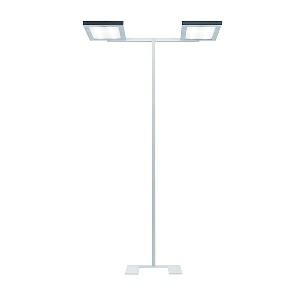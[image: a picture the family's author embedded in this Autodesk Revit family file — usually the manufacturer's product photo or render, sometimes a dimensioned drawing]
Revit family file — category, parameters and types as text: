
# Revit family: lavigo_-_dps_28000_vtl_r_g2_-twin-u_00810632_71ed
name_source: partatom
category: Lighting Fixtures
units: mm (PartAtom-declared; Revit-internal decimal feet)

## family parameters
Cut with Voids When Loaded = No
Host = Face
Light Source = No
Part Type = Normal
Room Calculation Point = No
Round Connector Dimension = Use Diameter
Shared = No

## types (1)
- LAVIGO - DPS 28000/VTL/R/G2 -TWIN-U (1 x LED VTL, 14250 lm, 3000-6500K)
    Apparent Load = 200 VA
    Approval mark = CE
    CIE Flux Codes = 60 87 97 12 100
    Color Rendering = 80-89
    Color Temperature = 3000-6500K
    Default Elevation = 1800 mm
    Description = DPS 28000/VTL/R/G2|Free-standing luminaire|light source: LED  3000-6500 K  Energy efficiency category A/A+/A++|work equipment: Electronic ballast|connected load: 220-240 V, 50/60 Hz|Power consumption: approx. 200 W|standby: approx. 0,50|power factor: approx. 0,966|luminous flux: 28500 lm|luminous efficacy: 142 lm/W|light distribution: Direct/indirect|direct ratio: approx. 12 %|color rendering index (CRI): >= 80|technology: Presence and daylight sensor control (PIR)|operation: Multi-function switch, Touch-LED|luminaire body|material: Steel/plastic|surface: Painted|colour: White|lamp cover: Acrylic (PMMA), Satine|tubular section|material: Steel tube|surface: Painted|Form: Tubular section upright|colour of tubular section: White|luminaire base|Form: C-form flat|weight (net): approx. 27.6 kg|mains lead: 3.00 m Mains plug CEE 7/VII|Fastening: Floor standing base|decorative contrast side parts: Flint grey|glare control: Prism aperture|luminance(L65): <= 3000 cd/m|unified glare rating(4H 8H): <=  16|special features: Luminaire head detachable, Direct light component with edge light and light-guide technology for homogenous light exit, Flicker-free, Integrated light and presence sensor PIR, Integrated light management for biodynamic light VTL, Retrofittable with TALK module, Separated, direct and indirect light individually adjustable|
    Frequency = 50 Hz, 60 Hz
    Height = 36 mm
    Lamp = 1 x LED VTL
    Lamp Light Flux = 14250 lm
    Lamp count = 1
    Length = 675 mm
    Luminous efficacy = 143 lm/W
    Manufacturer = Waldmann
    ModVariant = No
    Model = 00810632
    Mounting Place = Floor
    Mounting Type = Freestanding
    Number of Poles = 1
    OnlyDefault = Yes
    Power Factor = 1
    Product Name = LAVIGO - DPS 28000/VTL/R/G2 -TWIN-U
    Product group = Free standing luminaire
    ProductGroupID = 13
    Protection Class = Protection class I
    Protection Degree = IP 20
    RLX_Detail_Level = 1
    RLX_Emergency_Light_Flux = 0 lm
    RLX_Emergency_Type = 0
    RLX_Emergency_Type_DB = No
    RlxData = <blob elided: 37405 chars, md5=60cb5ebe>
    Socket = socket
    Standby Power = 0 W
    System Light Flux = 28500 lm
    System Power = 200 W
    Type Comments = Product without accessories
    Type Image = 121714000-00630753.jpg
    URL = http://relux.com
    VarID = ---
    Voltage = 230 V
    Voltage Range = 220-240 V
    Weight = 0.00 kg
    Width = 350 mm

## geometry (parser evidence)
native form markers: Blend x4, Sweep x20
no freeform markers — native parametric forms only
